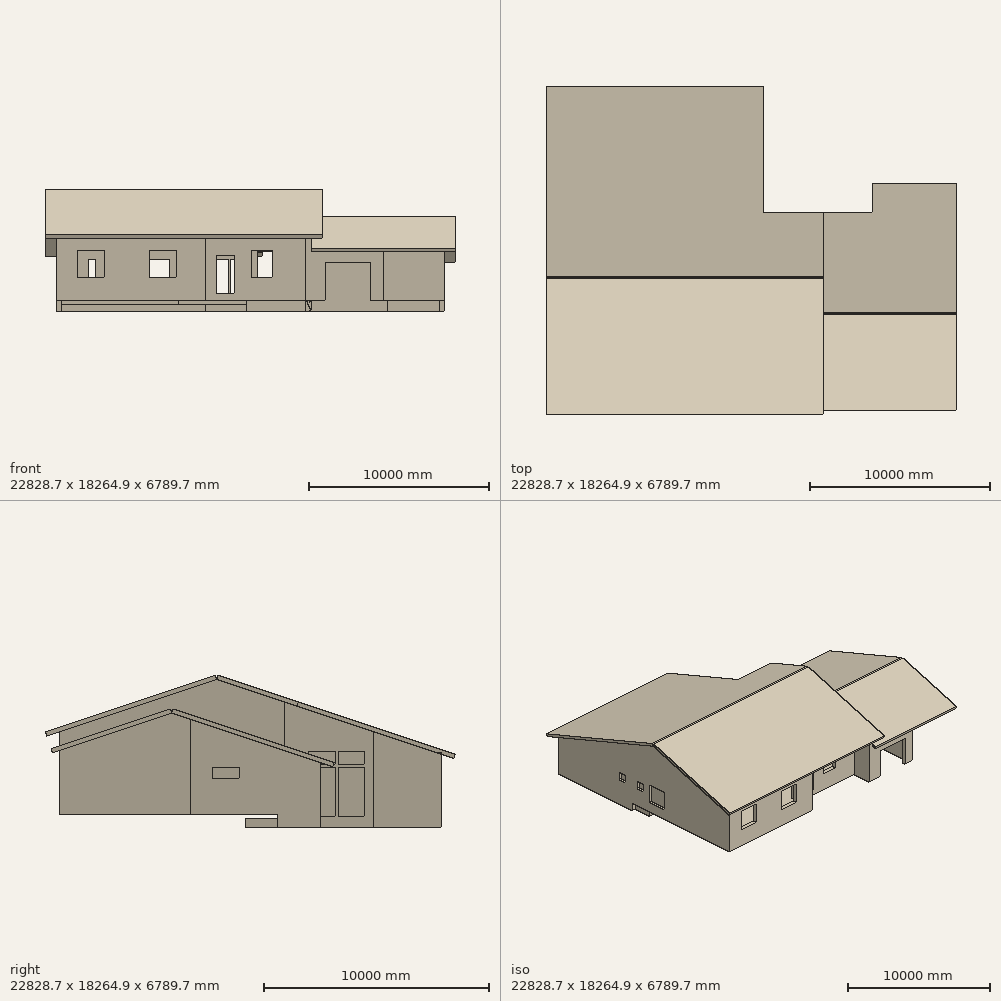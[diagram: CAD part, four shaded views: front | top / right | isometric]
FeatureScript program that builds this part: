
annotation { "Feature Type Name" : "Feature", "Feature Type Description" : "" }
export const myFeature = defineFeature(function(context is Context, id is Id, definition is map)
    precondition{}
    {
        {
            var Q0;
            Q0=qCreatedBy(makeId("Top.planeOp"),FACE);
            var sketch = newSketch(context, id + "F0", { "sketchPlane" : qUnion([Q0])});
            skLineSegment(sketch, "E0", {"start": v(0, 0) * mm, "end": v(0, 16400) * mm});
            skLineSegment(sketch, "E1", {"start": v(0, 16400) * mm, "end": v(6500, 16400) * mm});
            skLineSegment(sketch, "E2", {"start": v(6500, 16400) * mm, "end": v(6500, 13400) * mm});
            skLineSegment(sketch, "E3", {"start": v(6500, 13400) * mm, "end": v(10300, 13400) * mm});
            skLineSegment(sketch, "E4", {"start": v(10300, 13400) * mm, "end": v(10300, 9400) * mm});
            skLineSegment(sketch, "E5", {"start": v(10300, 9400) * mm, "end": v(13600, 9400) * mm});
            skLineSegment(sketch, "E6", {"start": v(13600, 9400) * mm, "end": v(13600, 1500) * mm});
            skLineSegment(sketch, "E7", {"start": v(13600, 1500) * mm, "end": v(7700, 1500) * mm});
            skLineSegment(sketch, "E8", {"start": v(7700, 1500) * mm, "end": v(7700, 0) * mm});
            skLineSegment(sketch, "E9", {"start": v(7700, 0) * mm, "end": v(0, 0) * mm});
            skSolve(sketch);
        }
        {
            var Q0;
            Q0=makeQuery(id+"F0.imprint","IMPRINT",FACE,{"disambiguationData":[TD([[makeQuery(id+"F0.imprint","IMPRINT",EDGE,{"derivedFrom":sQuery(id+"F0.wireOp",EDGE,"E0")}),-1.0]])]});
            var sketch = newSketch(context, id + "F1", { "sketchPlane" : qUnion([Q0])});
            skLineSegment(sketch, "E10.0", {"start": v(8000, -300) * mm, "end": v(-300, -300) * mm});
            skLineSegment(sketch, "E10.1", {"start": v(8000, 1200) * mm, "end": v(8000, -300) * mm});
            skLineSegment(sketch, "E10.2", {"start": v(-300, -300) * mm, "end": v(-300, 16700) * mm});
            skLineSegment(sketch, "E10.3", {"start": v(13900, 1200) * mm, "end": v(8000, 1200) * mm});
            skLineSegment(sketch, "E10.4", {"start": v(13900, 9700) * mm, "end": v(13900, 1200) * mm});
            skLineSegment(sketch, "E10.5", {"start": v(10600, 9700) * mm, "end": v(13900, 9700) * mm});
            skLineSegment(sketch, "E10.6", {"start": v(-300, 16700) * mm, "end": v(6800, 16700) * mm});
            skLineSegment(sketch, "E10.7", {"start": v(6800, 16700) * mm, "end": v(6800, 13700) * mm});
            skLineSegment(sketch, "E10.8", {"start": v(6800, 13700) * mm, "end": v(10600, 13700) * mm});
            skLineSegment(sketch, "E10.9", {"start": v(10600, 13700) * mm, "end": v(10600, 9700) * mm});
            skSolve(sketch);
        }
        {
            var Q0;
            Q0=makeQuery(id+"F0.imprint","IMPRINT",FACE,{"disambiguationData":[TD([[makeQuery(id+"F0.imprint","IMPRINT",EDGE,{"derivedFrom":sQuery(id+"F0.wireOp",EDGE,"E0")}),-1.0]])]});
            var sketch = newSketch(context, id + "F2", { "sketchPlane" : qUnion([Q0])});
            skLineSegment(sketch, "E11", {"start": v(13602.67, 9700) * mm, "end": v(17828.67, 9700) * mm});
            skLineSegment(sketch, "E12", {"start": v(17828.67, 9700) * mm, "end": v(17828.67, 11300) * mm});
            skLineSegment(sketch, "E13", {"start": v(17828.67, 11300) * mm, "end": v(21328.67, 11300) * mm});
            skLineSegment(sketch, "E14", {"start": v(21328.67, 11300) * mm, "end": v(21328.67, 5523) * mm});
            skLineSegment(sketch, "E15", {"start": v(21328.67, 5523) * mm, "end": v(17902.67, 5523) * mm});
            skLineSegment(sketch, "E16", {"start": v(17902.67, 5523) * mm, "end": v(17902.67, -300) * mm});
            skLineSegment(sketch, "E17", {"start": v(17902.67, -300) * mm, "end": v(13602.67, -300) * mm});
            skLineSegment(sketch, "E18", {"start": v(13602.67, -300) * mm, "end": v(13602.67, 9700) * mm});
            skLineSegment(sketch, "E19.0", {"start": v(21028.67, 10934.57) * mm, "end": v(21028.67, 5099.7) * mm, "construction": true});
            skSolve(sketch);
        }
        {
            var Q0;
            Q0=makeQuery(id+"F1.imprint","IMPRINT",FACE,{"disambiguationData":[TD([[makeQuery(id+"F1.imprint","IMPRINT",EDGE,{"derivedFrom":sQuery(id+"F1.wireOp",EDGE,"E10.0")}),-1.0]])]});
            var Q1;
            Q1=makeQuery(id+"F2.imprint","IMPRINT",FACE,{"disambiguationData":[TD([[makeQuery(id+"F2.imprint","IMPRINT",EDGE,{"derivedFrom":sQuery(id+"F2.wireOp",EDGE,"E11")}),-1.0]])]});
            extrude(context, id + "F3", {"entities" : qUnion([Q0, Q1]), "depth" : 10000 * mm});
        }
        {
            var Q0;
            Q0=makeQuery(id+"F3.opExtrude","CAP_FACE",FACE,{"disambiguationData":[OSD([sQuery(id+"F2.wireOp",EDGE,"E11"),sQuery(id+"F2.wireOp",EDGE,"E12"),sQuery(id+"F2.wireOp",EDGE,"E13"),sQuery(id+"F2.wireOp",EDGE,"E14"),sQuery(id+"F2.wireOp",EDGE,"E15"),sQuery(id+"F2.wireOp",EDGE,"E16"),sQuery(id+"F2.wireOp",EDGE,"E17"),sQuery(id+"F2.wireOp",EDGE,"E18")])],"isStart":false});
            var Q1;
            Q1=makeQuery(id+"F3.opExtrude","CAP_FACE",FACE,{"disambiguationData":[OSD([sQuery(id+"F2.wireOp",EDGE,"E11"),sQuery(id+"F2.wireOp",EDGE,"E12"),sQuery(id+"F2.wireOp",EDGE,"E13"),sQuery(id+"F2.wireOp",EDGE,"E14"),sQuery(id+"F2.wireOp",EDGE,"E15"),sQuery(id+"F2.wireOp",EDGE,"E16"),sQuery(id+"F2.wireOp",EDGE,"E17"),sQuery(id+"F2.wireOp",EDGE,"E18")])],"isStart":true});
            shell(context, id + "F4", {"entities" : qUnion([Q0, Q1]), "thickness" : 300 * mm});
        }
        {
            var Q0;
            Q0=makeQuery(id+"F3.opExtrude","SWEPT_FACE",FACE,{"disambiguationData":[OSD([sQuery(id+"F2.wireOp",EDGE,"E18")])]});
            var sketch = newSketch(context, id + "F5", { "sketchPlane" : qUnion([Q0])});
            skLineSegment(sketch, "E20.bottom", {"start": v(300, 0) * mm, "end": v(-9400, 0) * mm});
            skLineSegment(sketch, "E20.top", {"start": v(300, 600) * mm, "end": v(-9400, 600) * mm});
            skLineSegment(sketch, "E20.left", {"start": v(300, 0) * mm, "end": v(300, 600) * mm});
            skLineSegment(sketch, "E20.right", {"start": v(-9400, 0) * mm, "end": v(-9400, 600) * mm});
            skSolve(sketch);
        }
        {
            var Q0;
            Q0 = qSketchRegion(id + "F5", true);
            var Q1;
            Q1=makeQuery(id+"F3.opExtrude","SWEPT_FACE",FACE,{"disambiguationData":[OSD([sQuery(id+"F2.wireOp",EDGE,"E14")])]});
            extrude(context, id + "F6", {"entities" : qUnion([Q0]), "operationType" : NewBodyOperationType.REMOVE, "endBound" : BoundingType.UP_TO_SURFACE, "oppositeDirection" : true, "endBoundEntityFace" : qUnion([Q1]), "depth" : 25 * mm, "hasSecondDirection" : true, "secondDirectionBound" : SecondDirectionBoundingType.THROUGH_ALL, "secondDirectionOppositeDirection" : false, "secondDirectionDepth" : 25 * mm});
        }
        {
            var Q0;
            Q0=makeQuery(id+"F4.opShell","OFFSET_FACE",FACE,{"disambiguationData":[OSD([sQuery(id+"F2.wireOp",EDGE,"E18")])]});
            var sketch = newSketch(context, id + "F7", { "sketchPlane" : qUnion([Q0])});
            skLineSegment(sketch, "E21", {"start": v(4700, 10000) * mm, "end": v(4700, 6298.42) * mm, "construction": true});
            skLineSegment(sketch, "E22", {"start": v(-6543.16, 1353.36) * mm, "end": v(4700, 5100) * mm});
            skLineSegment(sketch, "E23.MirrorCS", {"start": v(15943.16, 1353.36) * mm, "end": v(4700, 5100) * mm});
            skLineSegment(sketch, "E24", {"start": v(-6543.16, 1353.36) * mm, "end": v(15943.16, 1353.36) * mm, "construction": true});
            skLineSegment(sketch, "E25", {"start": v(-6543.16, 1353.36) * mm, "end": v(-6543.16, 10000) * mm});
            skLineSegment(sketch, "E26", {"start": v(-6543.16, 10000) * mm, "end": v(15943.16, 10000) * mm});
            skLineSegment(sketch, "E27", {"start": v(15943.16, 10000) * mm, "end": v(15943.16, 1353.36) * mm});
            skSolve(sketch);
        }
        {
            var Q0;
            Q0 = qSketchRegion(id + "F7", true);
            extrude(context, id + "F8", {"entities" : qUnion([Q0]), "operationType" : NewBodyOperationType.REMOVE, "endBound" : BoundingType.THROUGH_ALL, "depth" : 25 * mm});
        }
        {
            var Q0;
            Q0=makeQuery(id+"F3.opExtrude","SWEPT_FACE",FACE,{"disambiguationData":[OSD([sQuery(id+"F1.wireOp",EDGE,"E10.2")])]});
            var sketch = newSketch(context, id + "F9", { "sketchPlane" : qUnion([Q0])});
            skLineSegment(sketch, "E28", {"start": v(-16700, 3267.63) * mm, "end": v(-6700, 6600) * mm});
            skLineSegment(sketch, "E29", {"start": v(-6700, 6600) * mm, "end": v(300, 4267.34) * mm});
            skLineSegment(sketch, "E30", {"start": v(300, 4267.34) * mm, "end": v(300, 10000) * mm});
            skLineSegment(sketch, "E31", {"start": v(300, 10000) * mm, "end": v(-16700, 10000) * mm});
            skLineSegment(sketch, "E32", {"start": v(-16700, 10000) * mm, "end": v(-16700, 3267.63) * mm});
            skLineSegment(sketch, "E33", {"start": v(-16700, 3267.63) * mm, "end": v(300, 3267.63) * mm, "construction": true});
            skLineSegment(sketch, "E34", {"start": v(300, 4267.34) * mm, "end": v(-16700, 4267.34) * mm, "construction": true});
            skSolve(sketch);
        }
        {
            var Q0;
            Q0 = qSketchRegion(id + "F9", true);
            var Q1;
            Q1=makeQuery(id+"F8.boolean.opBoolean","MERGE",FACE,{"derivedFrom":[makeQuery(id+"F4.opShell","OFFSET_FACE",FACE,{"disambiguationData":[OSD([sQuery(id+"F2.wireOp",EDGE,"E18")])]}),makeQuery(id+"F8.opExtrude","CAP_FACE",FACE,{"disambiguationData":[OSD([sQuery(id+"F7.wireOp",EDGE,"E22"),sQuery(id+"F7.wireOp",EDGE,"E23.MirrorCS"),sQuery(id+"F7.wireOp",EDGE,"E25"),sQuery(id+"F7.wireOp",EDGE,"E26"),sQuery(id+"F7.wireOp",EDGE,"E27")])],"isStart":true})]});
            extrude(context, id + "F10", {"entities" : qUnion([Q0]), "operationType" : NewBodyOperationType.REMOVE, "endBound" : BoundingType.UP_TO_SURFACE, "oppositeDirection" : true, "endBoundEntityFace" : qUnion([Q1]), "depth" : 25 * mm});
        }
        {
            var Q0;
            Q0=makeQuery(id+"F3.opExtrude","CAP_FACE",FACE,{"disambiguationData":[OSD([sQuery(id+"F0.wireOp",EDGE,"E0"),sQuery(id+"F0.wireOp",EDGE,"E1"),sQuery(id+"F0.wireOp",EDGE,"E2"),sQuery(id+"F0.wireOp",EDGE,"E3"),sQuery(id+"F0.wireOp",EDGE,"E4"),sQuery(id+"F0.wireOp",EDGE,"E5"),sQuery(id+"F0.wireOp",EDGE,"E6"),sQuery(id+"F0.wireOp",EDGE,"E7"),sQuery(id+"F0.wireOp",EDGE,"E8"),sQuery(id+"F0.wireOp",EDGE,"E9"),sQuery(id+"F1.wireOp",EDGE,"E10.0"),sQuery(id+"F1.wireOp",EDGE,"E10.1"),sQuery(id+"F1.wireOp",EDGE,"E10.2"),sQuery(id+"F1.wireOp",EDGE,"E10.3"),sQuery(id+"F1.wireOp",EDGE,"E10.4"),sQuery(id+"F1.wireOp",EDGE,"E10.5"),sQuery(id+"F1.wireOp",EDGE,"E10.6"),sQuery(id+"F1.wireOp",EDGE,"E10.7"),sQuery(id+"F1.wireOp",EDGE,"E10.8"),sQuery(id+"F1.wireOp",EDGE,"E10.9")])],"isStart":true});
            var sketch = newSketch(context, id + "F11", { "sketchPlane" : qUnion([Q0])});
            skLineSegment(sketch, "E35", {"start": v(0, -7993.08) * mm, "end": v(0, -16400) * mm});
            skLineSegment(sketch, "E36", {"start": v(0, -16400) * mm, "end": v(6500, -16400) * mm});
            skLineSegment(sketch, "E37", {"start": v(6500, -16400) * mm, "end": v(6500, -13400) * mm});
            skLineSegment(sketch, "E38", {"start": v(6500, -13400) * mm, "end": v(10300, -13400) * mm});
            skLineSegment(sketch, "E39", {"start": v(10300, -13400) * mm, "end": v(10300, -9400) * mm});
            skLineSegment(sketch, "E40", {"start": v(0, -7993.08) * mm, "end": v(8000, -7993.08) * mm});
            skLineSegment(sketch, "E41", {"start": v(8000, -7993.08) * mm, "end": v(8000, -9393.08) * mm});
            skPoint(sketch, "E42.orphan", {"position": v(0, -7993.08) * mm});
            skLineSegment(sketch, "E43", {"start": v(0, -16400) * mm, "end": v(0, -7993.08) * mm});
            skLineSegment(sketch, "E44", {"start": v(8000, -9393.08) * mm, "end": v(10300, -9400) * mm});
            skSolve(sketch);
        }
        {
            var Q0;
            Q0 = qSketchRegion(id + "F11", true);
            extrude(context, id + "F12", {"entities" : qUnion([Q0]), "oppositeDirection" : true, "depth" : 400 * mm});
        }
        {
            var Q0;
            Q0=makeQuery(id+"F6.boolean.opBoolean","COPY",FACE,{"disambiguationData":[TD([makeQuery(id+"F3.opExtrude","SWEPT_FACE",FACE,{"disambiguationData":[OSD([sQuery(id+"F1.wireOp",EDGE,"E10.0")])]})])],"derivedFrom":makeQuery(id+"F6.opExtrude","SWEPT_FACE",FACE,{"disambiguationData":[OSD([sQuery(id+"F5.wireOp",EDGE,"E20.top")])]})});
            var sketch = newSketch(context, id + "F13", { "sketchPlane" : qUnion([Q0])});
            skLineSegment(sketch, "E45", {"start": v(0, -9400) * mm, "end": v(0, -16400) * mm});
            skLineSegment(sketch, "E46", {"start": v(0, 0) * mm, "end": v(0, -7993.08) * mm});
            skLineSegment(sketch, "E47", {"start": v(13600, -9400) * mm, "end": v(13600, -1500) * mm});
            skLineSegment(sketch, "E48", {"start": v(8000, -9400) * mm, "end": v(13600, -9400) * mm});
            skLineSegment(sketch, "E49", {"start": v(13600, -1500) * mm, "end": v(7700, -1500) * mm});
            skLineSegment(sketch, "E50", {"start": v(7700, -1500) * mm, "end": v(7700, 0) * mm});
            skLineSegment(sketch, "E51", {"start": v(7700, 0) * mm, "end": v(0, 0) * mm});
            skLineSegment(sketch, "E52", {"start": v(8000, -9400) * mm, "end": v(8000, -7993.08) * mm});
            skLineSegment(sketch, "E53", {"start": v(8000, -7993.08) * mm, "end": v(0, -7993.08) * mm});
            skPoint(sketch, "E54.orphan", {"position": v(0, -9400) * mm});
            skSolve(sketch);
        }
        {
            var Q0;
            Q0 = qSketchRegion(id + "F13", true);
            extrude(context, id + "F14", {"entities" : qUnion([Q0]), "oppositeDirection" : true, "depth" : 400 * mm});
        }
        {
            var Q0;
            Q0=makeQuery(id+"F10.boolean.opBoolean","COPY",FACE,{"disambiguationData":[TD([makeQuery(id+"F3.opExtrude","SWEPT_FACE",FACE,{"disambiguationData":[OSD([sQuery(id+"F1.wireOp",EDGE,"E10.0")])]})])],"derivedFrom":makeQuery(id+"F10.opExtrude","SWEPT_FACE",FACE,{"disambiguationData":[OSD([sQuery(id+"F9.wireOp",EDGE,"E29")])]})});
            var sketch = newSketch(context, id + "F15", { "sketchPlane" : qUnion([Q0])});
            skLineSegment(sketch, "E55.bottom", {"start": v(-900, 8442.92) * mm, "end": v(14502.67, 8442.92) * mm});
            skLineSegment(sketch, "E55.top", {"start": v(-900, 464.49) * mm, "end": v(14502.67, 464.49) * mm});
            skLineSegment(sketch, "E55.left", {"start": v(-900, 8442.92) * mm, "end": v(-900, 464.49) * mm});
            skLineSegment(sketch, "E55.right", {"start": v(14502.67, 8442.92) * mm, "end": v(14502.67, 464.49) * mm});
            skSolve(sketch);
        }
        {
            var Q0;
            Q0 = qSketchRegion(id + "F15", true);
            extrude(context, id + "F16", {"entities" : qUnion([Q0]), "depth" : 200 * mm});
        }
        {
            var Q0;
            Q0=makeQuery(id+"F10.boolean.opBoolean","COPY",FACE,{"disambiguationData":[TD([makeQuery(id+"F3.opExtrude","SWEPT_FACE",FACE,{"disambiguationData":[OSD([sQuery(id+"F1.wireOp",EDGE,"E10.2")])]})])],"derivedFrom":makeQuery(id+"F10.opExtrude","SWEPT_FACE",FACE,{"disambiguationData":[OSD([sQuery(id+"F9.wireOp",EDGE,"E28")])]})});
            var sketch = newSketch(context, id + "F17", { "sketchPlane" : qUnion([Q0])});
            skLineSegment(sketch, "E56.bottom", {"start": v(14502.67, 4269.8) * mm, "end": v(-900, 4269.8) * mm});
            skLineSegment(sketch, "E56.top", {"start": v(11200, 15410.42) * mm, "end": v(-900, 15410.42) * mm});
            skLineSegment(sketch, "E56.left", {"start": v(14502.67, 4269.8) * mm, "end": v(14502.67, 8031.99) * mm});
            skLineSegment(sketch, "E56.right", {"start": v(-900, 4269.8) * mm, "end": v(-900, 15410.42) * mm});
            skLineSegment(sketch, "E57", {"start": v(14502.67, 8031.99) * mm, "end": v(11200, 8031.99) * mm});
            skLineSegment(sketch, "E58", {"start": v(11200, 8031.99) * mm, "end": v(11200, 15410.42) * mm});
            skSolve(sketch);
        }
        {
            var Q0;
            Q0 = qSketchRegion(id + "F17", true);
            extrude(context, id + "F18", {"entities" : qUnion([Q0]), "depth" : 200 * mm});
        }
        {
            var Q0;
            Q0=makeQuery(id+"F8.boolean.opBoolean","COPY",FACE,{"derivedFrom":makeQuery(id+"F8.opExtrude","SWEPT_FACE",FACE,{"disambiguationData":[OSD([sQuery(id+"F7.wireOp",EDGE,"E22")])]})});
            var sketch = newSketch(context, id + "F19", { "sketchPlane" : qUnion([Q0])});
            skLineSegment(sketch, "E59.bottom", {"start": v(13902.67, 6071.28) * mm, "end": v(21928.67, 6071.28) * mm});
            skLineSegment(sketch, "E59.top", {"start": v(13902.67, 464.49) * mm, "end": v(21928.67, 464.49) * mm});
            skLineSegment(sketch, "E59.left", {"start": v(13902.67, 6071.28) * mm, "end": v(13902.67, 464.49) * mm});
            skLineSegment(sketch, "E59.right", {"start": v(21928.67, 6071.28) * mm, "end": v(21928.67, 464.49) * mm});
            skSolve(sketch);
        }
        {
            var Q0;
            Q0 = qSketchRegion(id + "F19", true);
            extrude(context, id + "F20", {"entities" : qUnion([Q0]), "depth" : 200 * mm});
        }
        {
            var Q0;
            Q0=makeQuery(id+"F8.boolean.opBoolean","COPY",FACE,{"derivedFrom":makeQuery(id+"F8.opExtrude","SWEPT_FACE",FACE,{"disambiguationData":[OSD([sQuery(id+"F7.wireOp",EDGE,"E23.MirrorCS")])]})});
            var sketch = newSketch(context, id + "F21", { "sketchPlane" : qUnion([Q0])});
            skLineSegment(sketch, "E60.bottom", {"start": v(21928.67, 2846.6) * mm, "end": v(13902.67, 2846.6) * mm});
            skLineSegment(sketch, "E60.top", {"start": v(21928.67, 10403.4) * mm, "end": v(17228.67, 10403.4) * mm});
            skLineSegment(sketch, "E60.left", {"start": v(21928.67, 2846.6) * mm, "end": v(21928.67, 10403.4) * mm});
            skLineSegment(sketch, "E60.right", {"start": v(13902.67, 2846.6) * mm, "end": v(13902.67, 8716.9) * mm});
            skLineSegment(sketch, "E61", {"start": v(17228.67, 10403.4) * mm, "end": v(17228.67, 8716.9) * mm});
            skLineSegment(sketch, "E62", {"start": v(17228.67, 8716.9) * mm, "end": v(13902.67, 8716.9) * mm});
            skSolve(sketch);
        }
        {
            var Q0;
            Q0 = qSketchRegion(id + "F21", true);
            extrude(context, id + "F22", {"entities" : qUnion([Q0]), "depth" : 200 * mm});
        }
        {
            var Q0;
            Q0=makeQuery(id+"F3.opExtrude","SWEPT_FACE",FACE,{"disambiguationData":[OSD([sQuery(id+"F1.wireOp",EDGE,"E10.0")])]});
            var sketch = newSketch(context, id + "F23", { "sketchPlane" : qUnion([Q0])});
            skSolve(sketch);
        }
        {
            var Q0;
            {var subQ0=sQuery(id+"F1.wireOp",EDGE,"E10.0");Q0=makeQuery(id+"F23.imprint","IMPRINT",FACE,{"disambiguationData":[TD([[makeQuery(id+"F23.imprint","IMPRINT",EDGE,{"derivedFrom":makeQuery(id+"F3.opExtrude","SWEPT_EDGE",EDGE,{"disambiguationData":[OSD([subQ0,sQuery(id+"F1.wireOp",EDGE,"E10.1")])]})}),-1.0]])]});}
            var sketch = newSketch(context, id + "F24", { "sketchPlane" : qUnion([Q0])});
            skLineSegment(sketch, "E63.bottom", {"start": v(8600.28, 3100) * mm, "end": v(9600.28, 3100) * mm});
            skLineSegment(sketch, "E63.top", {"start": v(8600.28, 1000) * mm, "end": v(9600.28, 1000) * mm});
            skLineSegment(sketch, "E63.left", {"start": v(8600.28, 3100) * mm, "end": v(8600.28, 1000) * mm});
            skLineSegment(sketch, "E63.right", {"start": v(9600.28, 3100) * mm, "end": v(9600.28, 1000) * mm});
            skLineSegment(sketch, "E64.bottom", {"start": v(14702.67, 2700) * mm, "end": v(17202.67, 2700) * mm});
            skLineSegment(sketch, "E64.top", {"start": v(14702.67, 600) * mm, "end": v(17202.67, 600) * mm});
            skLineSegment(sketch, "E64.left", {"start": v(14702.67, 2700) * mm, "end": v(14702.67, 600) * mm});
            skLineSegment(sketch, "E64.right", {"start": v(17202.67, 2700) * mm, "end": v(17202.67, 600) * mm});
            skLineSegment(sketch, "E65.bottom", {"start": v(10550.28, 3400) * mm, "end": v(11750.28, 3400) * mm});
            skLineSegment(sketch, "E65.top", {"start": v(10550.28, 1900) * mm, "end": v(11750.28, 1900) * mm});
            skLineSegment(sketch, "E65.left", {"start": v(10550.28, 3400) * mm, "end": v(10550.28, 1900) * mm});
            skLineSegment(sketch, "E65.right", {"start": v(11750.28, 3400) * mm, "end": v(11750.28, 1900) * mm});
            skLineSegment(sketch, "E66.bottom", {"start": v(900, 1900) * mm, "end": v(2400, 1900) * mm});
            skLineSegment(sketch, "E66.top", {"start": v(900, 1900) * mm, "end": v(2400, 1900) * mm});
            skLineSegment(sketch, "E66.left", {"start": v(900, 1900) * mm, "end": v(900, 1900) * mm});
            skLineSegment(sketch, "E66.right", {"start": v(2400, 1900) * mm, "end": v(2400, 1900) * mm});
            skLineSegment(sketch, "E67.bottom", {"start": v(4900, 1900) * mm, "end": v(6400, 1900) * mm});
            skLineSegment(sketch, "E67.top", {"start": v(4900, 1900) * mm, "end": v(6400, 1900) * mm});
            skLineSegment(sketch, "E67.left", {"start": v(4900, 1900) * mm, "end": v(4900, 1900) * mm});
            skLineSegment(sketch, "E67.right", {"start": v(6400, 1900) * mm, "end": v(6400, 1900) * mm});
            skLineSegment(sketch, "E68", {"start": v(900, 1900) * mm, "end": v(900, 3400) * mm});
            skLineSegment(sketch, "E69", {"start": v(900, 3400) * mm, "end": v(2400, 3400) * mm});
            skLineSegment(sketch, "E70", {"start": v(2400, 3400) * mm, "end": v(2400, 1900) * mm});
            skLineSegment(sketch, "E71", {"start": v(4900, 1900) * mm, "end": v(4900, 3400) * mm});
            skLineSegment(sketch, "E72", {"start": v(4900, 3400) * mm, "end": v(6400, 3400) * mm});
            skLineSegment(sketch, "E73", {"start": v(6400, 3400) * mm, "end": v(6400, 1900) * mm});
            skSolve(sketch);
        }
        {
            var Q0;
            Q0 = qSketchRegion(id + "F24", true);
            var Q1;
            Q1=makeQuery(id+"F3.opExtrude","SWEPT_BODY",BODY,{"disambiguationData":[OSD([sQuery(id+"F0.wireOp",EDGE,"E0"),sQuery(id+"F0.wireOp",EDGE,"E1"),sQuery(id+"F0.wireOp",EDGE,"E2"),sQuery(id+"F0.wireOp",EDGE,"E3"),sQuery(id+"F0.wireOp",EDGE,"E4"),sQuery(id+"F0.wireOp",EDGE,"E5"),sQuery(id+"F0.wireOp",EDGE,"E6"),sQuery(id+"F0.wireOp",EDGE,"E7"),sQuery(id+"F0.wireOp",EDGE,"E8"),sQuery(id+"F0.wireOp",EDGE,"E9"),sQuery(id+"F1.wireOp",EDGE,"E10.0"),sQuery(id+"F1.wireOp",EDGE,"E10.1"),sQuery(id+"F1.wireOp",EDGE,"E10.2"),sQuery(id+"F1.wireOp",EDGE,"E10.3"),sQuery(id+"F1.wireOp",EDGE,"E10.4"),sQuery(id+"F1.wireOp",EDGE,"E10.5"),sQuery(id+"F1.wireOp",EDGE,"E10.6"),sQuery(id+"F1.wireOp",EDGE,"E10.7"),sQuery(id+"F1.wireOp",EDGE,"E10.8"),sQuery(id+"F1.wireOp",EDGE,"E10.9")])]});
            extrude(context, id + "F25", {"entities" : qUnion([Q0]), "operationType" : NewBodyOperationType.REMOVE, "oppositeDirection" : true, "endBoundEntityBody" : qUnion([Q1]), "depth" : 2000 * mm});
        }
        {
            var Q0;
            Q0=makeQuery(id+"F3.opExtrude","SWEPT_FACE",FACE,{"disambiguationData":[OSD([sQuery(id+"F2.wireOp",EDGE,"E14")])]});
            var sketch = newSketch(context, id + "F26", { "sketchPlane" : qUnion([Q0])});
            skLineSegment(sketch, "E74.bottom", {"start": v(6507.66, 2700) * mm, "end": v(7707.66, 2700) * mm});
            skLineSegment(sketch, "E74.top", {"start": v(6507.66, 2200) * mm, "end": v(7707.66, 2200) * mm});
            skLineSegment(sketch, "E74.left", {"start": v(6507.66, 2700) * mm, "end": v(6507.66, 2200) * mm});
            skLineSegment(sketch, "E74.right", {"start": v(7707.66, 2700) * mm, "end": v(7707.66, 2200) * mm});
            skSolve(sketch);
        }
        {
            var Q0;
            Q0 = qSketchRegion(id + "F26", true);
            extrude(context, id + "F27", {"entities" : qUnion([Q0]), "operationType" : NewBodyOperationType.REMOVE, "endBound" : BoundingType.UP_TO_NEXT, "oppositeDirection" : true, "depth" : 25 * mm});
        }
        {
            var Q0;
            Q0=makeQuery(id+"F3.opExtrude","SWEPT_FACE",FACE,{"disambiguationData":[OSD([sQuery(id+"F1.wireOp",EDGE,"E10.9")])]});
            var sketch = newSketch(context, id + "F28", { "sketchPlane" : qUnion([Q0])});
            skLineSegment(sketch, "E75.bottom", {"start": v(10800, 2700) * mm, "end": v(12000, 2700) * mm});
            skLineSegment(sketch, "E75.top", {"start": v(10800, 500) * mm, "end": v(12000, 500) * mm});
            skLineSegment(sketch, "E75.left", {"start": v(10800, 2700) * mm, "end": v(10800, 500) * mm});
            skLineSegment(sketch, "E75.right", {"start": v(12000, 2700) * mm, "end": v(12000, 500) * mm});
            skLineSegment(sketch, "E76.bottom", {"start": v(12100, 2700) * mm, "end": v(13300, 2700) * mm});
            skLineSegment(sketch, "E76.top", {"start": v(12100, 500) * mm, "end": v(13300, 500) * mm});
            skLineSegment(sketch, "E76.left", {"start": v(12100, 2700) * mm, "end": v(12100, 500) * mm});
            skLineSegment(sketch, "E76.right", {"start": v(13300, 2700) * mm, "end": v(13300, 500) * mm});
            skLineSegment(sketch, "E77.bottom", {"start": v(10800, 3400) * mm, "end": v(12000, 3400) * mm});
            skLineSegment(sketch, "E77.top", {"start": v(10800, 2800) * mm, "end": v(12000, 2800) * mm});
            skLineSegment(sketch, "E77.left", {"start": v(10800, 3400) * mm, "end": v(10800, 2800) * mm});
            skLineSegment(sketch, "E77.right", {"start": v(12000, 3400) * mm, "end": v(12000, 2800) * mm});
            skLineSegment(sketch, "E78.bottom", {"start": v(12100, 3400) * mm, "end": v(13300, 3400) * mm});
            skLineSegment(sketch, "E78.top", {"start": v(12100, 2800) * mm, "end": v(13300, 2800) * mm});
            skLineSegment(sketch, "E78.left", {"start": v(12100, 3400) * mm, "end": v(12100, 2800) * mm});
            skLineSegment(sketch, "E78.right", {"start": v(13300, 3400) * mm, "end": v(13300, 2800) * mm});
            skSolve(sketch);
        }
        {
            var Q0;
            Q0 = qSketchRegion(id + "F28", true);
            extrude(context, id + "F29", {"entities" : qUnion([Q0]), "operationType" : NewBodyOperationType.REMOVE, "endBound" : BoundingType.UP_TO_NEXT, "oppositeDirection" : true, "depth" : 25 * mm});
        }
        {
            var Q0;
            Q0=makeQuery(id+"F3.opExtrude","SWEPT_FACE",FACE,{"disambiguationData":[OSD([sQuery(id+"F1.wireOp",EDGE,"E10.6")])]});
            var sketch = newSketch(context, id + "F30", { "sketchPlane" : qUnion([Q0])});
            skLineSegment(sketch, "E79.bottom", {"start": v(-6024.74, 2900) * mm, "end": v(-4824.74, 2900) * mm});
            skLineSegment(sketch, "E79.top", {"start": v(-6024.74, 700) * mm, "end": v(-4824.74, 700) * mm});
            skLineSegment(sketch, "E79.left", {"start": v(-6024.74, 2900) * mm, "end": v(-6024.74, 700) * mm});
            skLineSegment(sketch, "E79.right", {"start": v(-4824.74, 2900) * mm, "end": v(-4824.74, 700) * mm});
            skLineSegment(sketch, "E80.bottom", {"start": v(-1896.11, 2900) * mm, "end": v(-1496.11, 2900) * mm});
            skLineSegment(sketch, "E80.top", {"start": v(-1896.11, 700) * mm, "end": v(-1496.11, 700) * mm});
            skLineSegment(sketch, "E80.left", {"start": v(-1896.11, 2900) * mm, "end": v(-1896.11, 700) * mm});
            skLineSegment(sketch, "E80.right", {"start": v(-1496.11, 2900) * mm, "end": v(-1496.11, 700) * mm});
            skLineSegment(sketch, "E81.bottom", {"start": v(-10300, 2900) * mm, "end": v(-9400, 2900) * mm});
            skLineSegment(sketch, "E81.top", {"start": v(-10300, 700) * mm, "end": v(-9400, 700) * mm});
            skLineSegment(sketch, "E81.left", {"start": v(-10300, 2900) * mm, "end": v(-10300, 700) * mm});
            skLineSegment(sketch, "E81.right", {"start": v(-9400, 2900) * mm, "end": v(-9400, 700) * mm});
            skLineSegment(sketch, "E82.bottom", {"start": v(-9300, 2900) * mm, "end": v(-8100, 2900) * mm});
            skLineSegment(sketch, "E82.top", {"start": v(-9300, 700) * mm, "end": v(-8100, 700) * mm});
            skLineSegment(sketch, "E82.left", {"start": v(-9300, 2900) * mm, "end": v(-9300, 700) * mm});
            skLineSegment(sketch, "E82.right", {"start": v(-8100, 2900) * mm, "end": v(-8100, 700) * mm});
            skLineSegment(sketch, "E83.bottom", {"start": v(-7900, 2900) * mm, "end": v(-7000, 2900) * mm});
            skLineSegment(sketch, "E83.top", {"start": v(-7900, 600) * mm, "end": v(-7000, 600) * mm});
            skLineSegment(sketch, "E83.left", {"start": v(-7900, 2900) * mm, "end": v(-7900, 600) * mm});
            skLineSegment(sketch, "E83.right", {"start": v(-7000, 2900) * mm, "end": v(-7000, 600) * mm});
            skLineSegment(sketch, "E84.bottom", {"start": v(-13400, 3364.56) * mm, "end": v(-12200, 3364.56) * mm});
            skLineSegment(sketch, "E84.top", {"start": v(-13400, 1164.56) * mm, "end": v(-12200, 1164.56) * mm});
            skLineSegment(sketch, "E84.left", {"start": v(-13400, 3364.56) * mm, "end": v(-13400, 1164.56) * mm});
            skLineSegment(sketch, "E84.right", {"start": v(-12200, 3364.56) * mm, "end": v(-12200, 1164.56) * mm});
            skLineSegment(sketch, "E85.bottom", {"start": v(-12100, 3364.56) * mm, "end": v(-10900, 3364.56) * mm});
            skLineSegment(sketch, "E85.top", {"start": v(-12100, 1164.56) * mm, "end": v(-10900, 1164.56) * mm});
            skLineSegment(sketch, "E85.left", {"start": v(-12100, 3364.56) * mm, "end": v(-12100, 1164.56) * mm});
            skLineSegment(sketch, "E85.right", {"start": v(-10900, 3364.56) * mm, "end": v(-10900, 1164.56) * mm});
            skSolve(sketch);
        }
        {
            var Q0;
            Q0 = qSketchRegion(id + "F30", true);
            var Q1;
            Q1=makeQuery(id+"F3.opExtrude","SWEPT_FACE",FACE,{"disambiguationData":[OSD([sQuery(id+"F0.wireOp",EDGE,"E1")])]});
            var Q2;
            Q2=makeQuery(id+"F14.opExtrude","SWEPT_BODY",BODY,{"disambiguationData":[OSD([sQuery(id+"F13.wireOp",EDGE,"E46"),sQuery(id+"F13.wireOp",EDGE,"E47"),sQuery(id+"F13.wireOp",EDGE,"E48"),sQuery(id+"F13.wireOp",EDGE,"E49"),sQuery(id+"F13.wireOp",EDGE,"E50"),sQuery(id+"F13.wireOp",EDGE,"E51"),sQuery(id+"F13.wireOp",EDGE,"E52"),sQuery(id+"F13.wireOp",EDGE,"E53")])]});
            extrude(context, id + "F31", {"entities" : qUnion([Q0]), "operationType" : NewBodyOperationType.REMOVE, "oppositeDirection" : true, "endBoundEntityFace" : qUnion([Q1]), "endBoundEntityBody" : qUnion([Q2]), "depth" : 7300 * mm});
        }
        {
            var Q0;
            {var subQ7=sQuery(id+"F9.wireOp",EDGE,"E28");Q0=makeQuery(id+"F9.imprint","IMPRINT",FACE,{"disambiguationData":[TD([[makeQuery(id+"F9.imprint","IMPRINT",EDGE,{"derivedFrom":subQ7}),-1.0]])]});}
            var sketch = newSketch(context, id + "F32", { "sketchPlane" : qUnion([Q0])});
            skLineSegment(sketch, "E86.bottom", {"start": v(-7700, 2800) * mm, "end": v(-6200, 2800) * mm});
            skLineSegment(sketch, "E86.top", {"start": v(-7700, 1400) * mm, "end": v(-6200, 1400) * mm});
            skLineSegment(sketch, "E86.left", {"start": v(-7700, 2800) * mm, "end": v(-7700, 1400) * mm});
            skLineSegment(sketch, "E86.right", {"start": v(-6200, 2800) * mm, "end": v(-6200, 1400) * mm});
            skLineSegment(sketch, "E87.bottom", {"start": v(-8900, 2600) * mm, "end": v(-8300, 2600) * mm});
            skLineSegment(sketch, "E87.top", {"start": v(-8900, 2000) * mm, "end": v(-8300, 2000) * mm});
            skLineSegment(sketch, "E87.left", {"start": v(-8900, 2600) * mm, "end": v(-8900, 2000) * mm});
            skLineSegment(sketch, "E87.right", {"start": v(-8300, 2600) * mm, "end": v(-8300, 2000) * mm});
            skLineSegment(sketch, "E88.bottom", {"start": v(-10700, 2600) * mm, "end": v(-10100, 2600) * mm});
            skLineSegment(sketch, "E88.top", {"start": v(-10700, 2000) * mm, "end": v(-10100, 2000) * mm});
            skLineSegment(sketch, "E88.left", {"start": v(-10700, 2600) * mm, "end": v(-10700, 2000) * mm});
            skLineSegment(sketch, "E88.right", {"start": v(-10100, 2600) * mm, "end": v(-10100, 2000) * mm});
            skSolve(sketch);
        }
        {
            var Q0;
            Q0 = qSketchRegion(id + "F32", true);
            extrude(context, id + "F33", {"entities" : qUnion([Q0]), "operationType" : NewBodyOperationType.REMOVE, "oppositeDirection" : true, "depth" : 200 * mm});
        }
    });
